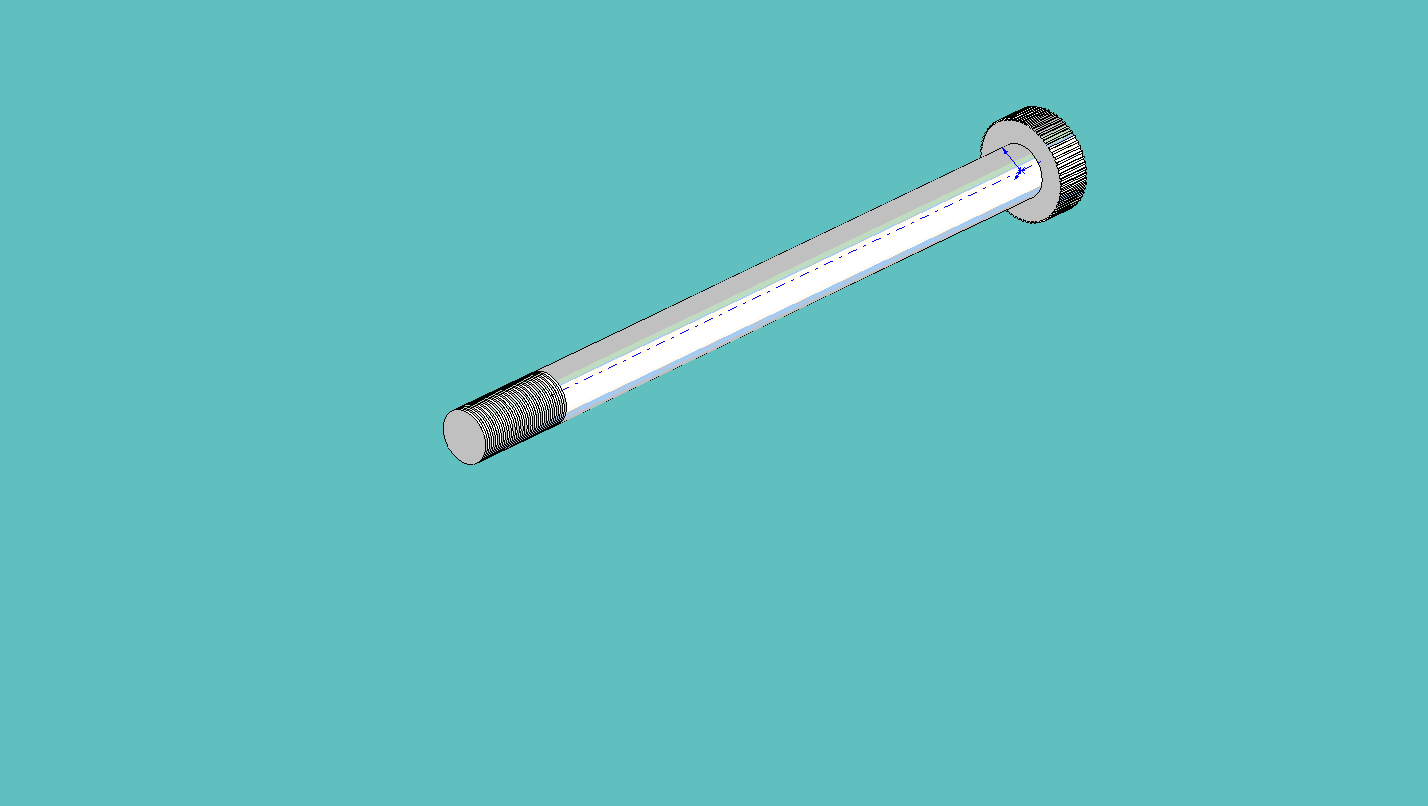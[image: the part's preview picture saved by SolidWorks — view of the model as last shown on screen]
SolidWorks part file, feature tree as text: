
SOLIDWORKS PART (.sldprt)
format: sldprt  version: not decoded by parser v0  size: 351,232 bytes
history: native  units: mm
features: sketch x5, extrude x3, material x1, cut_extrude x1, chamfer x1, pattern_circular x1, cut_revolve x1, pattern_linear x1 (+13 scaffold rows collapsed)
feature tree (27):
  scaffold x13  (default folders/planes/origin — collapsed)
  material  "Material <not specified>"
  sketch  "Sketch1"  dims[D1=18.288mm]
  extrude  "Extrude1"  Depth=6.35mm
  sketch  "Sketch2"  dims[D1=12.7mm]
  cut_extrude  "Cut-Extrude1"  Depth=3.81mm
  chamfer  "Chamfer1"  Distance=0.508mm Angle=45deg
  sketch  "Sketch3"  dims[D1=9.906mm]
  extrude  "Extrude2"  Depth=138.43mm
  sketch  "Sketch4"
  extrude  "Extrude3"  [1 undecoded]
  pattern_circular  "CirPattern1"  Count=60 Angle=360deg
  sketch  "Sketch5"
  cut_revolve  "Cut-Revolve1"  Angle=360deg
  pattern_linear  "LPattern1"  Count1=21 Count2=1 Spacing1=0.978mm Spacing2=50mm
decode coverage: 10 of 13 modeling features carry decoded parameters
note: 1 parameter value undecoded
note: suppression state not decoded; provenance and decode notes live in map.json
